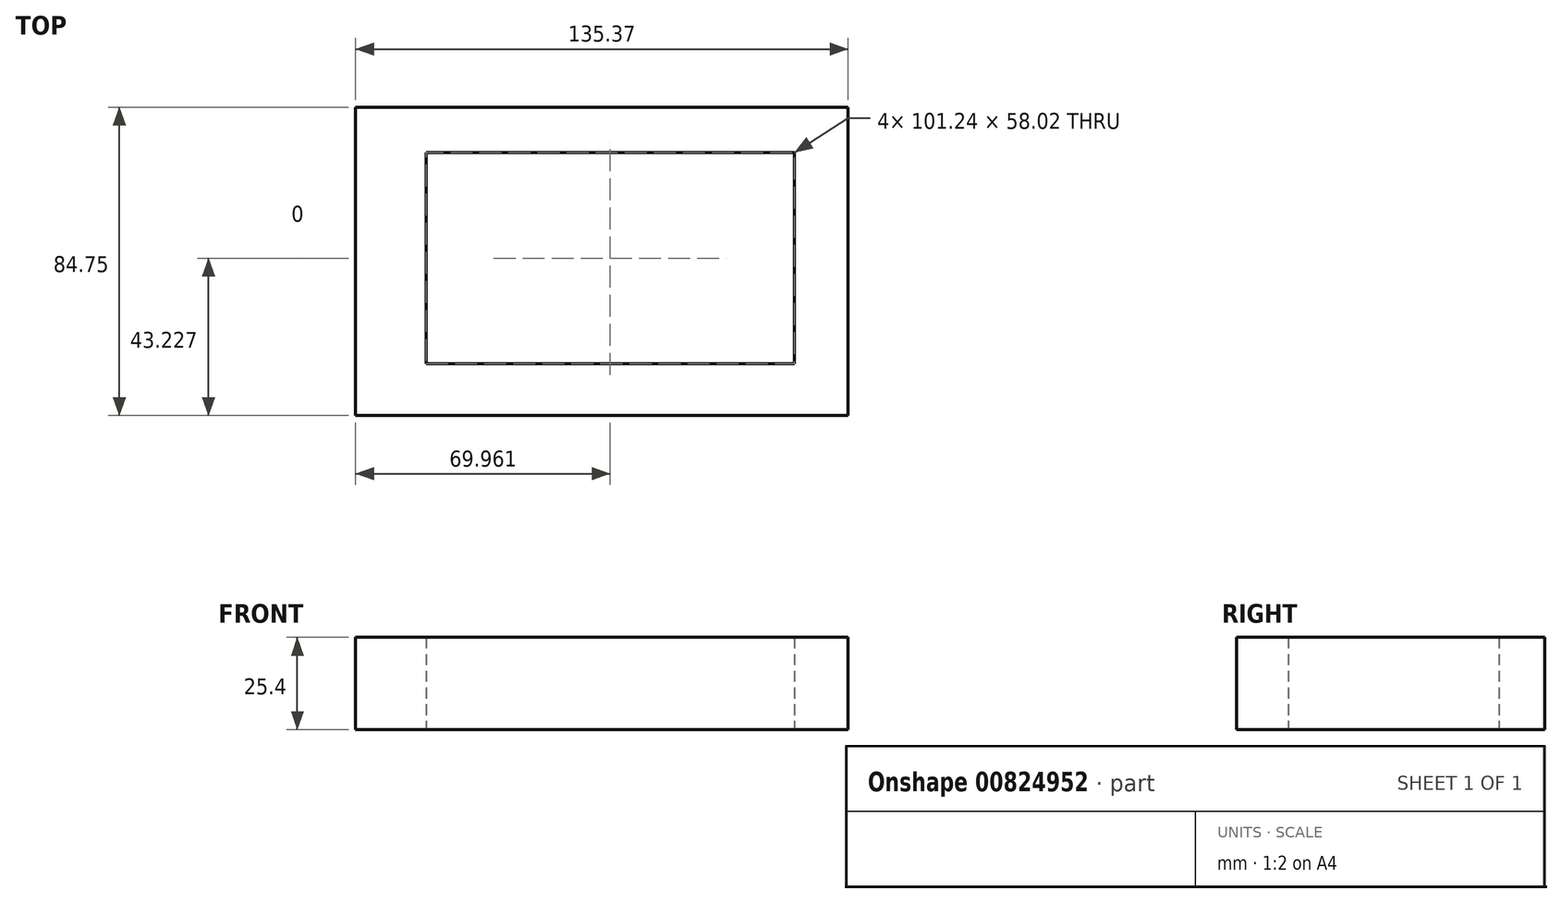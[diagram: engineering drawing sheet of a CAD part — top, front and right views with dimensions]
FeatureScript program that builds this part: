
annotation { "Feature Type Name" : "Feature", "Feature Type Description" : "" }
export const myFeature = defineFeature(function(context is Context, id is Id, definition is map)
    precondition{}
    {
        {
            var Q0;
            Q0=qCreatedBy(makeId("Top.planeOp"),FACE);
            var sketch = newSketch(context, id + "F0", { "sketchPlane" : qUnion([Q0])});
            skLineSegment(sketch, "E0.bottom", {"start": v(-68.16, 40.48) * mm, "end": v(67.21, 40.48) * mm});
            skLineSegment(sketch, "E0.top", {"start": v(-68.16, -44.27) * mm, "end": v(67.21, -44.27) * mm});
            skLineSegment(sketch, "E0.left", {"start": v(-68.16, 40.48) * mm, "end": v(-68.16, -44.27) * mm});
            skLineSegment(sketch, "E0.right", {"start": v(67.21, 40.48) * mm, "end": v(67.21, -44.27) * mm});
            skLineSegment(sketch, "E1.bottom", {"start": v(-48.82, 27.97) * mm, "end": v(52.42, 27.97) * mm});
            skLineSegment(sketch, "E1.top", {"start": v(-48.82, -30.05) * mm, "end": v(52.42, -30.05) * mm});
            skLineSegment(sketch, "E1.left", {"start": v(-48.82, 27.97) * mm, "end": v(-48.82, -30.05) * mm});
            skLineSegment(sketch, "E1.right", {"start": v(52.42, 27.97) * mm, "end": v(52.42, -30.05) * mm});
            skSolve(sketch);
        }
        {
            var Q0;
            Q0=makeQuery(id+"F0.imprint","IMPRINT",FACE,{"disambiguationData":[TD([[makeQuery(id+"F0.imprint","IMPRINT",EDGE,{"derivedFrom":sQuery(id+"F0.wireOp",EDGE,"E0.bottom")}),-1.0]])]});
            extrude(context, id + "F1", {"entities" : qUnion([Q0]), "depth" : 25.4 * mm, "offsetDistance" : 25.4 * mm});
        }
    });
